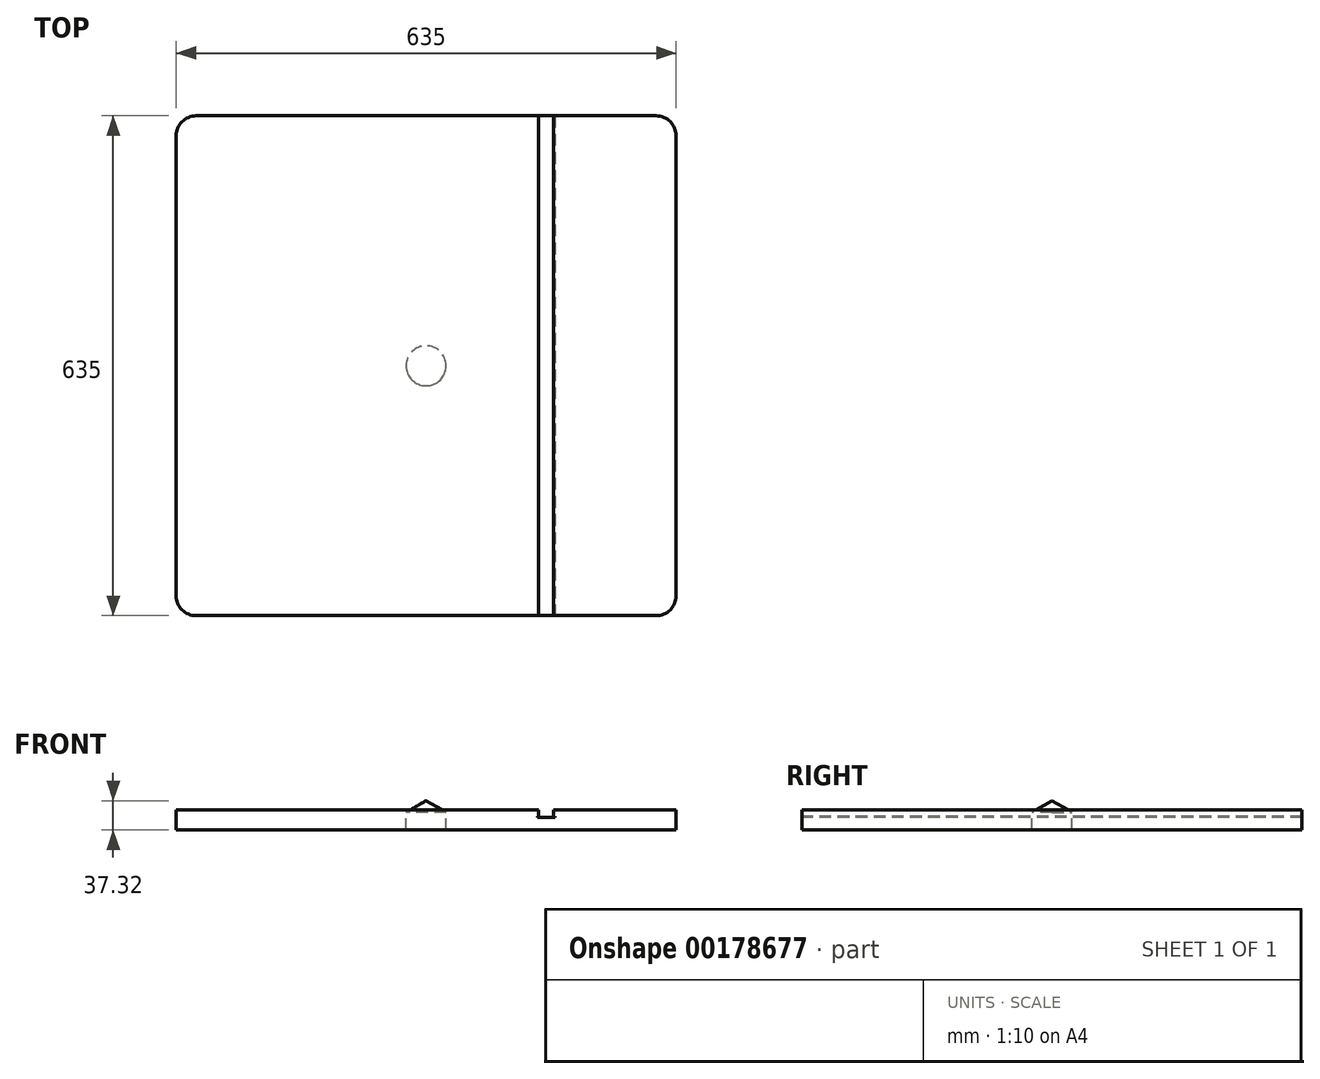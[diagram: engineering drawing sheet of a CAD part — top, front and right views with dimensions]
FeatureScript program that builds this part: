
annotation { "Feature Type Name" : "Feature", "Feature Type Description" : "" }
export const myFeature = defineFeature(function(context is Context, id is Id, definition is map)
    precondition{}
    {
        {
            var Q0;
            Q0=qCreatedBy(makeId("Top.planeOp"),FACE);
            var sketch = newSketch(context, id + "F0", { "sketchPlane" : qUnion([Q0])});
            skLineSegment(sketch, "E0.bottom", {"start": v(-292.1, 317.5) * mm, "end": v(292.1, 317.5) * mm});
            skLineSegment(sketch, "E0.top", {"start": v(-292.1, -317.5) * mm, "end": v(292.1, -317.5) * mm});
            skLineSegment(sketch, "E0.left", {"start": v(-317.5, 292.1) * mm, "end": v(-317.5, -292.1) * mm});
            skLineSegment(sketch, "E0.right", {"start": v(317.5, 292.1) * mm, "end": v(317.5, -292.1) * mm});
            skPoint(sketch, "E1.visualSharp", {"position": v(-317.5, 317.5) * mm});
            skArc(sketch, "E1.filletArc", {"start": v(-292.1, 317.5) * mm, "mid": v(-310.06, 310.06) * mm, "end": v(-317.5, 292.1) * mm});
            skPoint(sketch, "E2.visualSharp", {"position": v(-317.5, -317.5) * mm});
            skArc(sketch, "E2.filletArc", {"start": v(-317.5, -292.1) * mm, "mid": v(-310.06, -310.06) * mm, "end": v(-292.1, -317.5) * mm});
            skPoint(sketch, "E3.visualSharp", {"position": v(317.5, -317.5) * mm});
            skArc(sketch, "E3.filletArc", {"start": v(292.1, -317.5) * mm, "mid": v(310.06, -310.06) * mm, "end": v(317.5, -292.1) * mm});
            skPoint(sketch, "E4.visualSharp", {"position": v(317.5, 317.5) * mm});
            skArc(sketch, "E4.filletArc", {"start": v(317.5, 292.1) * mm, "mid": v(310.06, 310.06) * mm, "end": v(292.1, 317.5) * mm});
            skSolve(sketch);
        }
        {
            var Q0;
            Q0 = qSketchRegion(id + "F0", true);
            extrude(context, id + "F1", {"entities" : qUnion([Q0]), "depth" : 25.4 * mm});
        }
        {
            var Q0;
            Q0=qCreatedBy(makeId("Right.planeOp"),FACE);
            var sketch = newSketch(context, id + "F2", { "sketchPlane" : qUnion([Q0])});
            skLineSegment(sketch, "E5", {"start": v(0, 37.32) * mm, "end": v(-25.4, 22.65) * mm});
            skLineSegment(sketch, "E6", {"start": v(-25.4, 22.65) * mm, "end": v(-25.4, 0) * mm});
            skLineSegment(sketch, "E7", {"start": v(-25.4, 0) * mm, "end": v(0, 0) * mm});
            skLineSegment(sketch, "E8", {"start": v(0, 37.32) * mm, "end": v(0, 0) * mm});
            skLineSegment(sketch, "E9.0", {"start": v(292.1, 25.4) * mm, "end": v(-292.1, 25.4) * mm});
            skPoint(sketch, "E10", {"position": v(-20.64, 25.4) * mm});
            skPoint(sketch, "E11", {"position": v(0, 25.4) * mm});
            skSolve(sketch);
        }
        {
            var Q0;
            Q0 = qSketchRegion(id + "F2", true);
            var Q1;
            Q1=sQuery(id+"F2.wireOp",EDGE,"E8");
            revolve(context, id + "F3", {"entities" : qUnion([Q0]), "axis" : qUnion([Q1]), "revolveType" : RevolveType.FULL});
        }
        {
            var Q0;
            Q0=makeQuery(id+"F1.opExtrude","SWEPT_FACE",FACE,{"disambiguationData":[OSD([sQuery(id+"F0.wireOp",EDGE,"E0.top")])]});
            var sketch = newSketch(context, id + "F4", { "sketchPlane" : qUnion([Q0])});
            skLineSegment(sketch, "E12", {"start": v(142.88, 25.4) * mm, "end": v(142.88, 17.46) * mm});
            skLineSegment(sketch, "E13", {"start": v(142.88, 17.46) * mm, "end": v(141.29, 17.46) * mm});
            skLineSegment(sketch, "E14", {"start": v(141.29, 17.46) * mm, "end": v(141.29, 15.88) * mm});
            skLineSegment(sketch, "E15", {"start": v(141.29, 15.88) * mm, "end": v(163.51, 15.88) * mm});
            skLineSegment(sketch, "E16", {"start": v(163.51, 15.88) * mm, "end": v(163.51, 17.46) * mm});
            skLineSegment(sketch, "E17", {"start": v(163.51, 17.46) * mm, "end": v(161.93, 17.46) * mm});
            skLineSegment(sketch, "E18", {"start": v(161.93, 17.46) * mm, "end": v(161.93, 25.4) * mm});
            skLineSegment(sketch, "E19", {"start": v(161.93, 25.4) * mm, "end": v(142.88, 25.4) * mm});
            skPoint(sketch, "E20.0", {"position": v(0, 0) * mm});
            skPoint(sketch, "E21", {"position": v(152.4, 15.88) * mm});
            skSolve(sketch);
        }
        {
            var Q0;
            Q0=makeQuery(id+"F4.imprint","IMPRINT",FACE,{"disambiguationData":[TD([[makeQuery(id+"F4.imprint","IMPRINT",EDGE,{"derivedFrom":sQuery(id+"F4.wireOp",EDGE,"E12")}),1.0]])]});
            extrude(context, id + "F5", {"entities" : qUnion([Q0]), "operationType" : NewBodyOperationType.REMOVE, "endBound" : BoundingType.THROUGH_ALL, "oppositeDirection" : true, "depth" : 25.4 * mm});
        }
    });
